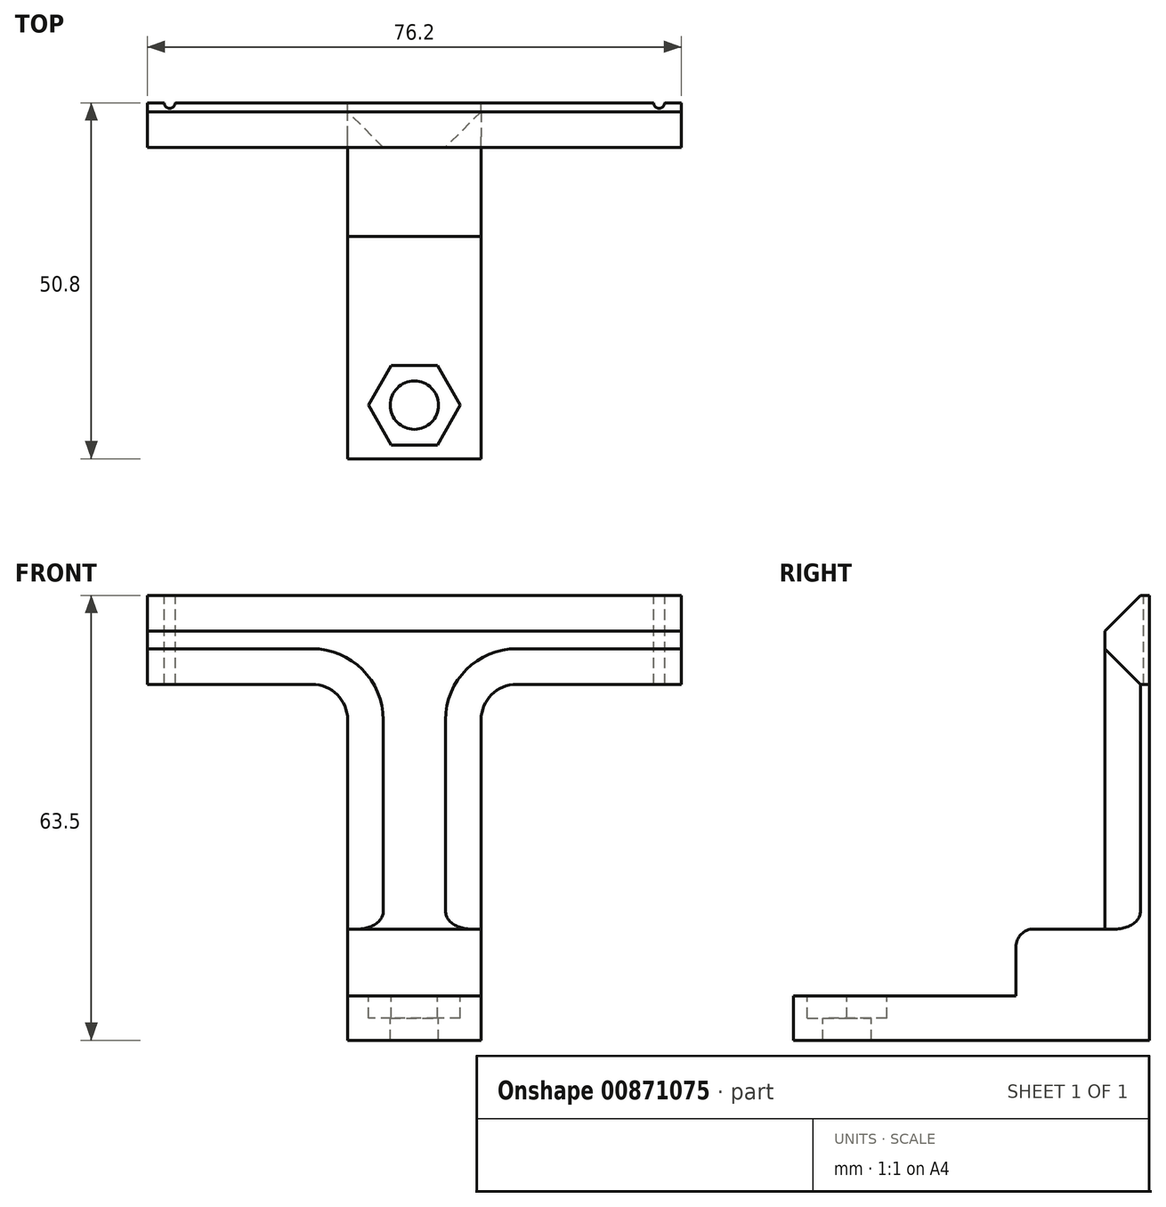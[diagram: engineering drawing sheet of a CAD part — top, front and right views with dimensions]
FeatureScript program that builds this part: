
annotation { "Feature Type Name" : "Feature", "Feature Type Description" : "" }
export const myFeature = defineFeature(function(context is Context, id is Id, definition is map)
    precondition{}
    {
        {
            var Q0;
            Q0=qCreatedBy(makeId("Front.planeOp"),FACE);
            var sketch = newSketch(context, id + "F0", { "sketchPlane" : qUnion([Q0])});
            skLineSegment(sketch, "E0", {"start": v(-38.1, 57.15) * mm, "end": v(-38.1, 44.45) * mm});
            skLineSegment(sketch, "E1", {"start": v(-38.1, 44.45) * mm, "end": v(-9.53, 44.45) * mm});
            skLineSegment(sketch, "E2", {"start": v(-9.53, 44.45) * mm, "end": v(-9.53, 0) * mm});
            skLineSegment(sketch, "E3", {"start": v(-9.52, 0) * mm, "end": v(0, 0) * mm});
            skLineSegment(sketch, "E4", {"start": v(0, 0) * mm, "end": v(9.52, 0) * mm});
            skLineSegment(sketch, "E5", {"start": v(9.52, 0) * mm, "end": v(9.52, 44.45) * mm});
            skLineSegment(sketch, "E6", {"start": v(9.52, 44.45) * mm, "end": v(38.1, 44.45) * mm});
            skLineSegment(sketch, "E7", {"start": v(38.1, 44.45) * mm, "end": v(38.1, 57.15) * mm});
            skLineSegment(sketch, "E8", {"start": v(38.1, 57.15) * mm, "end": v(-38.1, 57.15) * mm});
            skLineSegment(sketch, "E9", {"start": v(-38.1, 50.8) * mm, "end": v(38.1, 50.8) * mm, "construction": true});
            skSolve(sketch);
        }
        {
            var Q0;
            Q0=makeQuery(id+"F0.imprint","IMPRINT",FACE,{"disambiguationData":[TD([[makeQuery(id+"F0.imprint","IMPRINT",EDGE,{"derivedFrom":sQuery(id+"F0.wireOp",EDGE,"E0")}),1.0]])]});
            extrude(context, id + "F1", {"entities" : qUnion([Q0]), "depth" : 6.35 * mm, "offsetDistance" : 25.4 * mm});
        }
        {
            var Q0;
            Q0=makeQuery(id+"F1.opExtrude","SWEPT_FACE",FACE,{"disambiguationData":[OSD([sQuery(id+"F0.wireOp",EDGE,"E3"),sQuery(id+"F0.wireOp",EDGE,"E4")])]});
            var sketch = newSketch(context, id + "F2", { "sketchPlane" : qUnion([Q0])});
            skLineSegment(sketch, "E10.bottom", {"start": v(-9.53, 0) * mm, "end": v(9.52, 0) * mm});
            skLineSegment(sketch, "E10.top", {"start": v(-9.53, 50.8) * mm, "end": v(9.52, 50.8) * mm});
            skLineSegment(sketch, "E10.left", {"start": v(-9.53, 0) * mm, "end": v(-9.53, 50.8) * mm});
            skLineSegment(sketch, "E10.right", {"start": v(9.52, 0) * mm, "end": v(9.52, 50.8) * mm});
            skCircle(sketch, "E11", {"center": v(0, 43.15) * mm, "radius": 3.45 * mm});
            skSolve(sketch);
        }
        {
            var Q0;
            Q0 = qSketchRegion(id + "F2", true);
            extrude(context, id + "F3", {"entities" : qUnion([Q0]), "operationType" : NewBodyOperationType.ADD, "depth" : 6.35 * mm, "offsetDistance" : 25.4 * mm});
        }
        {
            var Q0;
            Q0=makeQuery(id+"F1.opExtrude","CAP_FACE",FACE,{"disambiguationData":[OSD([sQuery(id+"F0.wireOp",EDGE,"E0"),sQuery(id+"F0.wireOp",EDGE,"E1"),sQuery(id+"F0.wireOp",EDGE,"E2"),sQuery(id+"F0.wireOp",EDGE,"E3"),sQuery(id+"F0.wireOp",EDGE,"E4"),sQuery(id+"F0.wireOp",EDGE,"E5"),sQuery(id+"F0.wireOp",EDGE,"E6"),sQuery(id+"F0.wireOp",EDGE,"E7"),sQuery(id+"F0.wireOp",EDGE,"E8")])],"isStart":false});
            var sketch = newSketch(context, id + "F4", { "sketchPlane" : qUnion([Q0])});
            skLineSegment(sketch, "E12", {"start": v(38.1, 50.8) * mm, "end": v(-38.1, 50.8) * mm, "construction": true});
            skLineSegment(sketch, "E13.bottom", {"start": v(9.52, 0) * mm, "end": v(-9.53, 0) * mm});
            skLineSegment(sketch, "E13.top", {"start": v(9.52, 9.52) * mm, "end": v(-9.53, 9.52) * mm});
            skLineSegment(sketch, "E13.left", {"start": v(9.52, 0) * mm, "end": v(9.52, 9.52) * mm});
            skLineSegment(sketch, "E13.right", {"start": v(-9.53, 0) * mm, "end": v(-9.53, 9.52) * mm});
            skSolve(sketch);
        }
        {
            var Q0;
            Q0 = qSketchRegion(id + "F4", true);
            extrude(context, id + "F5", {"entities" : qUnion([Q0]), "operationType" : NewBodyOperationType.ADD, "depth" : 12.7 * mm, "offsetDistance" : 25.4 * mm});
        }
        {
            var Q0;
            Q0=makeQuery(id+"F5.opExtrude","CAP_EDGE",EDGE,{"disambiguationData":[OSD([sQuery(id+"F4.wireOp",EDGE,"E13.top")])],"isStart":false});
            var Q1;
            Q1=makeQuery(id+"F5.opExtrude","CAP_EDGE",EDGE,{"disambiguationData":[OSD([sQuery(id+"F4.wireOp",EDGE,"E13.bottom")])],"isStart":false});
            fillet(context, id + "F6", {"entities" : qUnion([Q0, Q1]), "radius" : 2.54 * mm, "tangentPropagation" : true, "allowEdgeOverflow" : false});
        }
        {
            var Q0;
            Q0=makeQuery(id+"F3.opExtrude","CAP_FACE",FACE,{"disambiguationData":[OSD([sQuery(id+"F2.wireOp",EDGE,"E10.bottom"),sQuery(id+"F2.wireOp",EDGE,"E10.top"),sQuery(id+"F2.wireOp",EDGE,"E10.left"),sQuery(id+"F2.wireOp",EDGE,"E10.right"),sQuery(id+"F2.wireOp",EDGE,"E11")])],"isStart":true});
            var sketch = newSketch(context, id + "F7", { "sketchPlane" : qUnion([Q0])});
            skCircle(sketch, "E14.cCircle", {"center": v(0, -43.15) * mm, "radius": 5.68 * mm, "construction": true});
            skLineSegment(sketch, "E14.0", {"start": v(-3.28, -48.84) * mm, "end": v(-6.56, -43.15) * mm});
            skLineSegment(sketch, "E14.1", {"start": v(-6.56, -43.15) * mm, "end": v(-3.28, -37.47) * mm});
            skLineSegment(sketch, "E14.2", {"start": v(-3.28, -37.47) * mm, "end": v(3.28, -37.47) * mm});
            skLineSegment(sketch, "E14.3", {"start": v(3.28, -37.47) * mm, "end": v(6.56, -43.15) * mm});
            skLineSegment(sketch, "E14.4", {"start": v(6.56, -43.15) * mm, "end": v(3.28, -48.84) * mm});
            skLineSegment(sketch, "E14.5", {"start": v(3.28, -48.84) * mm, "end": v(-3.28, -48.84) * mm});
            skPoint(sketch, "E14.0.midPoint", {"position": v(-4.92, -46) * mm});
            skSolve(sketch);
        }
        {
            var Q0;
            Q0=makeQuery(id+"F7.imprint","IMPRINT",FACE,{"disambiguationData":[TD([[makeQuery(id+"F7.imprint","IMPRINT",EDGE,{"derivedFrom":sQuery(id+"F7.wireOp",EDGE,"E14.0")}),-1.0]])]});
            var Q1;
            Q1 = qConstructionFilter(qBodyType(qCreatedBy(id + "F7" ,EDGE), BodyType.WIRE), ConstructionObject.NO);
            extrude(context, id + "F8", {"entities" : qUnion([Q0]), "operationType" : NewBodyOperationType.REMOVE, "surfaceEntities" : qUnion([Q1]), "oppositeDirection" : true, "depth" : 3.17 * mm, "offsetDistance" : 25.4 * mm});
        }
        {
            var Q0;
            Q0=makeQuery(id+"F1.opExtrude","SWEPT_EDGE",EDGE,{"disambiguationData":[OSD([sQuery(id+"F0.wireOp",EDGE,"E1"),sQuery(id+"F0.wireOp",EDGE,"E2")])]});
            var Q1;
            Q1=makeQuery(id+"F1.opExtrude","SWEPT_EDGE",EDGE,{"disambiguationData":[OSD([sQuery(id+"F0.wireOp",EDGE,"E5"),sQuery(id+"F0.wireOp",EDGE,"E6")])]});
            fillet(context, id + "F9", {"entities" : qUnion([Q0, Q1]), "radius" : 5.08 * mm, "tangentPropagation" : true, "allowEdgeOverflow" : false});
        }
        {
            var Q0;
            Q0=makeQuery(id+"F1.opExtrude","CAP_EDGE",EDGE,{"disambiguationData":[OSD([sQuery(id+"F0.wireOp",EDGE,"E8")])],"isStart":false});
            var Q1;
            Q1=makeQuery(id+"F1.opExtrude","CAP_EDGE",EDGE,{"disambiguationData":[OSD([sQuery(id+"F0.wireOp",EDGE,"E1")])],"isStart":false});
            var Q2;
            {var subQ0=sQuery(id+"F0.wireOp",EDGE,"E6");var subQ1=sQuery(id+"F0.wireOp",EDGE,"E5");Q2=makeQuery(id+"F9.opFillet","BLEND_EDGE",EDGE,{"blendedFrom":[makeQuery(id+"F1.opExtrude","SWEPT_EDGE",EDGE,{"disambiguationData":[OSD([subQ1,subQ0])]}),makeQuery(id+"F1.opExtrude","CAP_FACE",FACE,{"disambiguationData":[OSD([sQuery(id+"F0.wireOp",EDGE,"E0"),sQuery(id+"F0.wireOp",EDGE,"E1"),sQuery(id+"F0.wireOp",EDGE,"E2"),sQuery(id+"F0.wireOp",EDGE,"E3"),sQuery(id+"F0.wireOp",EDGE,"E4"),subQ1,subQ0,sQuery(id+"F0.wireOp",EDGE,"E7"),sQuery(id+"F0.wireOp",EDGE,"E8")])],"isStart":false})],"blendedInto":[makeQuery(id+"F1.opExtrude","CAP_FACE",FACE,{"disambiguationData":[OSD([sQuery(id+"F0.wireOp",EDGE,"E0"),sQuery(id+"F0.wireOp",EDGE,"E1"),sQuery(id+"F0.wireOp",EDGE,"E2"),sQuery(id+"F0.wireOp",EDGE,"E3"),sQuery(id+"F0.wireOp",EDGE,"E4"),subQ1,subQ0,sQuery(id+"F0.wireOp",EDGE,"E7"),sQuery(id+"F0.wireOp",EDGE,"E8")])],"isStart":false})]});}
            chamfer(context, id + "F10", {"entities" : qUnion([Q0, Q1, Q2]), "width" : 5.08 * mm, "tangentPropagation" : true});
        }
        {
            var Q0;
            Q0=makeQuery(id+"F10.opChamfer","BLEND_EDGE",EDGE,{"blendedFrom":[makeQuery(id+"F1.opExtrude","CAP_EDGE",EDGE,{"disambiguationData":[OSD([sQuery(id+"F0.wireOp",EDGE,"E2")])],"isStart":false}),makeQuery(id+"F5.opExtrude","SWEPT_FACE",FACE,{"disambiguationData":[OSD([sQuery(id+"F4.wireOp",EDGE,"E13.top")])]})],"blendedInto":[makeQuery(id+"F5.opExtrude","SWEPT_FACE",FACE,{"disambiguationData":[OSD([sQuery(id+"F4.wireOp",EDGE,"E13.top")])]})]});
            var Q1;
            Q1=makeQuery(id+"F10.opChamfer","BLEND_EDGE",EDGE,{"blendedFrom":[makeQuery(id+"F1.opExtrude","CAP_EDGE",EDGE,{"disambiguationData":[OSD([sQuery(id+"F0.wireOp",EDGE,"E5")])],"isStart":false}),makeQuery(id+"F5.opExtrude","SWEPT_FACE",FACE,{"disambiguationData":[OSD([sQuery(id+"F4.wireOp",EDGE,"E13.top")])]})],"blendedInto":[makeQuery(id+"F5.opExtrude","SWEPT_FACE",FACE,{"disambiguationData":[OSD([sQuery(id+"F4.wireOp",EDGE,"E13.top")])]})]});
            var Q2;
            Q2=makeQuery(id+"F5.opExtrude","CAP_EDGE",EDGE,{"disambiguationData":[OSD([sQuery(id+"F4.wireOp",EDGE,"E13.top")])],"isStart":true});
            fillet(context, id + "F11", {"entities" : qUnion([Q0, Q1, Q2]), "radius" : 2.54 * mm, "tangentPropagation" : true, "allowEdgeOverflow" : false});
        }
        {
            var Q0;
            Q0=makeQuery(id+"F1.opExtrude","SWEPT_FACE",FACE,{"disambiguationData":[OSD([sQuery(id+"F0.wireOp",EDGE,"E8")])]});
            var sketch = newSketch(context, id + "F12", { "sketchPlane" : qUnion([Q0])});
            skCircle(sketch, "E15", {"center": v(34.93, 0) * mm, "radius": 0.8 * mm});
            skLineSegment(sketch, "E16", {"start": v(0, 37.49) * mm, "end": v(0, -57.99) * mm, "construction": true});
            skCircle(sketch, "E17.MirrorC", {"center": v(-34.93, 0) * mm, "radius": 0.8 * mm});
            skSolve(sketch);
        }
        {
            var Q0;
            Q0 = qSketchRegion(id + "F12", true);
            extrude(context, id + "F13", {"entities" : qUnion([Q0]), "operationType" : NewBodyOperationType.REMOVE, "oppositeDirection" : true, "depth" : 25.4 * mm, "offsetDistance" : 25.4 * mm});
        }
    });
